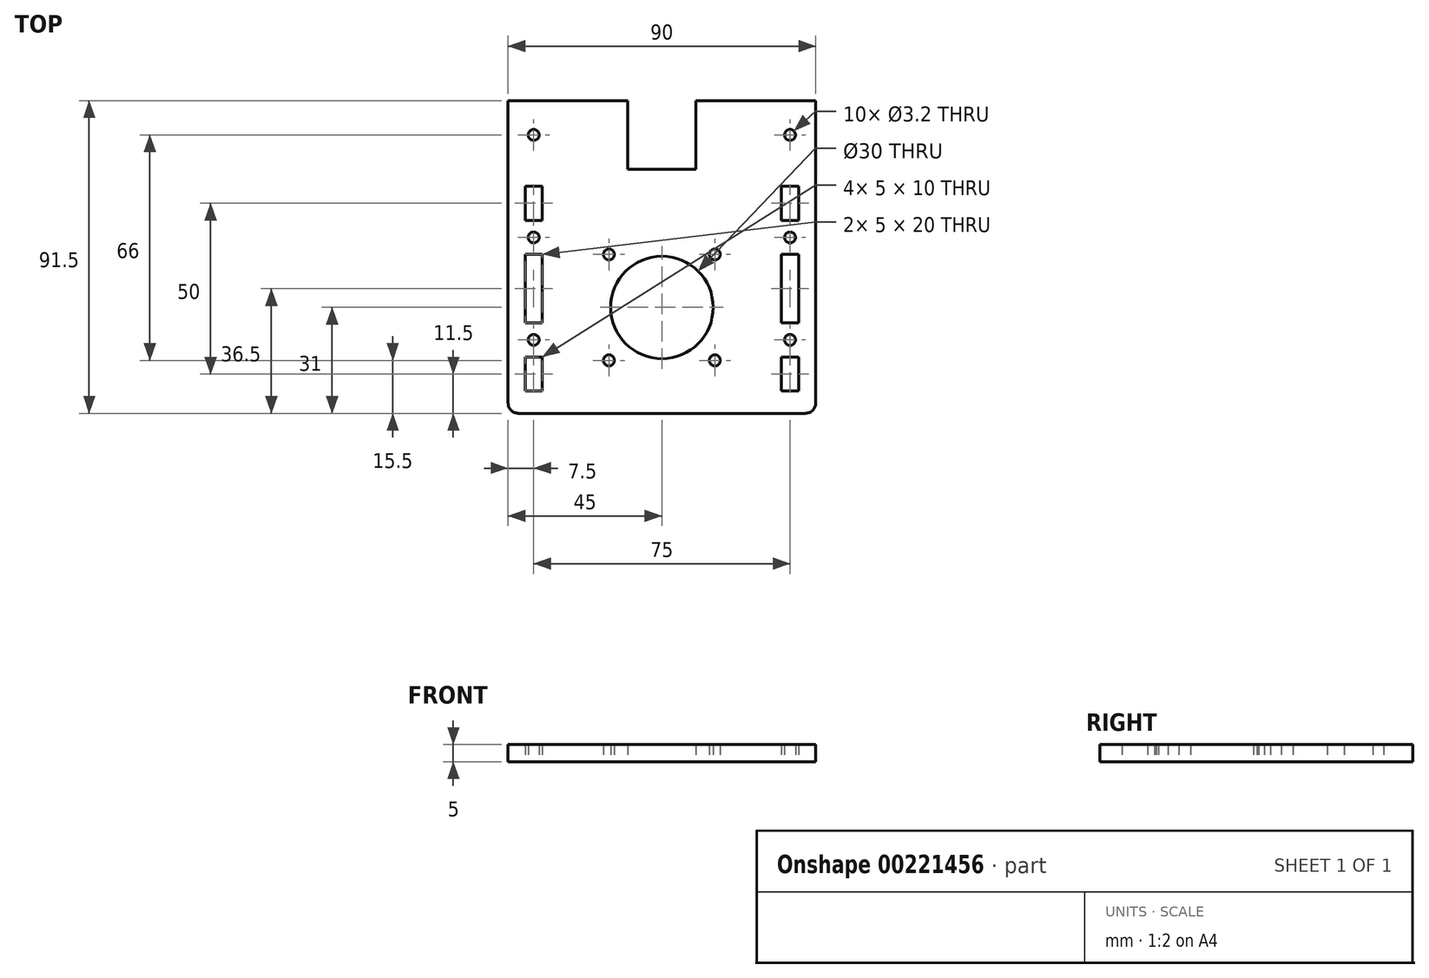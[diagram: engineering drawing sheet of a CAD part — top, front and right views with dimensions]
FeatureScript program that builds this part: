
annotation { "Feature Type Name" : "Feature", "Feature Type Description" : "" }
export const myFeature = defineFeature(function(context is Context, id is Id, definition is map)
    precondition{}
    {
        {
            assignVariable(context, id + "F0", {"name" : "thickness", "anyValue" : 5 * mm});
        }
        {
            var Q0;
            Q0=qCreatedBy(makeId("Top.planeOp"),FACE);
            var sketch = newSketch(context, id + "F1", { "sketchPlane" : qUnion([Q0])});
            skLineSegment(sketch, "E0", {"start": v(0, 0) * mm, "end": v(0, -20) * mm});
            skLineSegment(sketch, "E1", {"start": v(0, -20) * mm, "end": v(20, -20) * mm});
            skLineSegment(sketch, "E2", {"start": v(20, -20) * mm, "end": v(20, 0) * mm});
            skLineSegment(sketch, "E3", {"start": v(0, 0) * mm, "end": v(-35, 0) * mm});
            skCircle(sketch, "E4", {"center": v(10, -60.5) * mm, "radius": 15 * mm});
            skPoint(sketch, "E4.centerSnap0", {"position": v(10, -20) * mm});
            skCircle(sketch, "E5", {"center": v(25.5, -76) * mm, "radius": 1.6 * mm});
            skCircle(sketch, "E6.1.0", {"center": v(25.5, -45) * mm, "radius": 1.6 * mm});
            skCircle(sketch, "E6.2.0", {"center": v(-5.5, -45) * mm, "radius": 1.6 * mm});
            skCircle(sketch, "E6.3.0", {"center": v(-5.5, -76) * mm, "radius": 1.6 * mm});
            skLineSegment(sketch, "E7", {"start": v(-35, 0) * mm, "end": v(-35, -88.5) * mm});
            skLineSegment(sketch, "E8", {"start": v(-32, -91.5) * mm, "end": v(52, -91.5) * mm});
            skLineSegment(sketch, "E9", {"start": v(55, -88.5) * mm, "end": v(55, 0) * mm});
            skLineSegment(sketch, "E10", {"start": v(55, 0) * mm, "end": v(20, 0) * mm});
            skLineSegment(sketch, "E11.bottom", {"start": v(31, -39.5) * mm, "end": v(-11, -39.5) * mm, "construction": true});
            skLineSegment(sketch, "E11.top", {"start": v(31, -81.5) * mm, "end": v(-11, -81.5) * mm, "construction": true});
            skLineSegment(sketch, "E11.left", {"start": v(31, -39.5) * mm, "end": v(31, -81.5) * mm, "construction": true});
            skLineSegment(sketch, "E11.right", {"start": v(-11, -39.5) * mm, "end": v(-11, -81.5) * mm, "construction": true});
            skLineSegment(sketch, "E12.bottom", {"start": v(-30, -85) * mm, "end": v(-25, -85) * mm});
            skLineSegment(sketch, "E12.top", {"start": v(-30, -75) * mm, "end": v(-25, -75) * mm});
            skLineSegment(sketch, "E12.left", {"start": v(-30, -85) * mm, "end": v(-30, -75) * mm});
            skLineSegment(sketch, "E12.right", {"start": v(-25, -85) * mm, "end": v(-25, -75) * mm});
            skLineSegment(sketch, "E13.bottom", {"start": v(-30, -65) * mm, "end": v(-25, -65) * mm});
            skLineSegment(sketch, "E13.top", {"start": v(-30, -45) * mm, "end": v(-25, -45) * mm});
            skLineSegment(sketch, "E13.left", {"start": v(-30, -65) * mm, "end": v(-30, -45) * mm});
            skLineSegment(sketch, "E13.right", {"start": v(-25, -65) * mm, "end": v(-25, -45) * mm});
            skLineSegment(sketch, "E14.bottom", {"start": v(-30, -35) * mm, "end": v(-25, -35) * mm});
            skLineSegment(sketch, "E14.top", {"start": v(-30, -25) * mm, "end": v(-25, -25) * mm});
            skLineSegment(sketch, "E14.left", {"start": v(-30, -35) * mm, "end": v(-30, -25) * mm});
            skLineSegment(sketch, "E14.right", {"start": v(-25, -35) * mm, "end": v(-25, -25) * mm});
            skLineSegment(sketch, "E15", {"start": v(10, -91.5) * mm, "end": v(10, -20) * mm, "construction": true});
            skLineSegment(sketch, "E16.MirrorCS", {"start": v(50, -75) * mm, "end": v(45, -75) * mm});
            skLineSegment(sketch, "E17.MirrorCS", {"start": v(45, -85) * mm, "end": v(45, -75) * mm});
            skLineSegment(sketch, "E18.MirrorCS", {"start": v(50, -45) * mm, "end": v(45, -45) * mm});
            skLineSegment(sketch, "E19.MirrorCS", {"start": v(50, -65) * mm, "end": v(50, -45) * mm});
            skLineSegment(sketch, "E20.MirrorCS", {"start": v(50, -35) * mm, "end": v(45, -35) * mm});
            skLineSegment(sketch, "E21.MirrorCS", {"start": v(45, -35) * mm, "end": v(45, -25) * mm});
            skLineSegment(sketch, "E22.MirrorCS", {"start": v(50, -35) * mm, "end": v(50, -25) * mm});
            skLineSegment(sketch, "E23.MirrorCS", {"start": v(50, -25) * mm, "end": v(45, -25) * mm});
            skLineSegment(sketch, "E24.MirrorCS", {"start": v(45, -65) * mm, "end": v(45, -45) * mm});
            skLineSegment(sketch, "E25.MirrorCS", {"start": v(50, -65) * mm, "end": v(45, -65) * mm});
            skLineSegment(sketch, "E26.MirrorCS", {"start": v(50, -85) * mm, "end": v(50, -75) * mm});
            skLineSegment(sketch, "E27.MirrorCS", {"start": v(50, -85) * mm, "end": v(45, -85) * mm});
            skCircle(sketch, "E28", {"center": v(-27.5, -40) * mm, "radius": 1.6 * mm});
            skPoint(sketch, "E28.centerSnap0", {"position": v(-27.5, -35) * mm});
            skCircle(sketch, "E29", {"center": v(-27.5, -70) * mm, "radius": 1.6 * mm});
            skPoint(sketch, "E29.centerSnap0", {"position": v(-27.5, -65) * mm});
            skCircle(sketch, "E30.MirrorC", {"center": v(47.5, -40) * mm, "radius": 1.6 * mm});
            skCircle(sketch, "E31.MirrorC", {"center": v(47.5, -70) * mm, "radius": 1.6 * mm});
            skCircle(sketch, "E32", {"center": v(-27.5, -10) * mm, "radius": 1.6 * mm});
            skPoint(sketch, "E32.centerSnap0", {"position": v(0, -10) * mm});
            skCircle(sketch, "E33", {"center": v(47.5, -10) * mm, "radius": 1.6 * mm});
            skPoint(sketch, "E33.centerSnap0", {"position": v(20, -10) * mm});
            skLineSegment(sketch, "E34", {"start": v(-27.5, -10) * mm, "end": v(47.5, -10) * mm, "construction": true});
            skPoint(sketch, "E35", {"position": v(10, -10) * mm});
            skPoint(sketch, "E36.visualSharp", {"position": v(-35, -91.5) * mm});
            skArc(sketch, "E36.filletArc", {"start": v(-35, -88.5) * mm, "mid": v(-34.12, -90.62) * mm, "end": v(-32, -91.5) * mm});
            skPoint(sketch, "E37.visualSharp", {"position": v(55, -91.5) * mm});
            skArc(sketch, "E37.filletArc", {"start": v(52, -91.5) * mm, "mid": v(54.12, -90.62) * mm, "end": v(55, -88.5) * mm});
            skSolve(sketch);
        }
        {
            var Q0;
            Q0 = qSketchRegion(id + "F1", true);
            extrude(context, id + "F2", {"entities" : qUnion([Q0]), "depth" : getVariable(context, 'thickness')});
        }
    });
